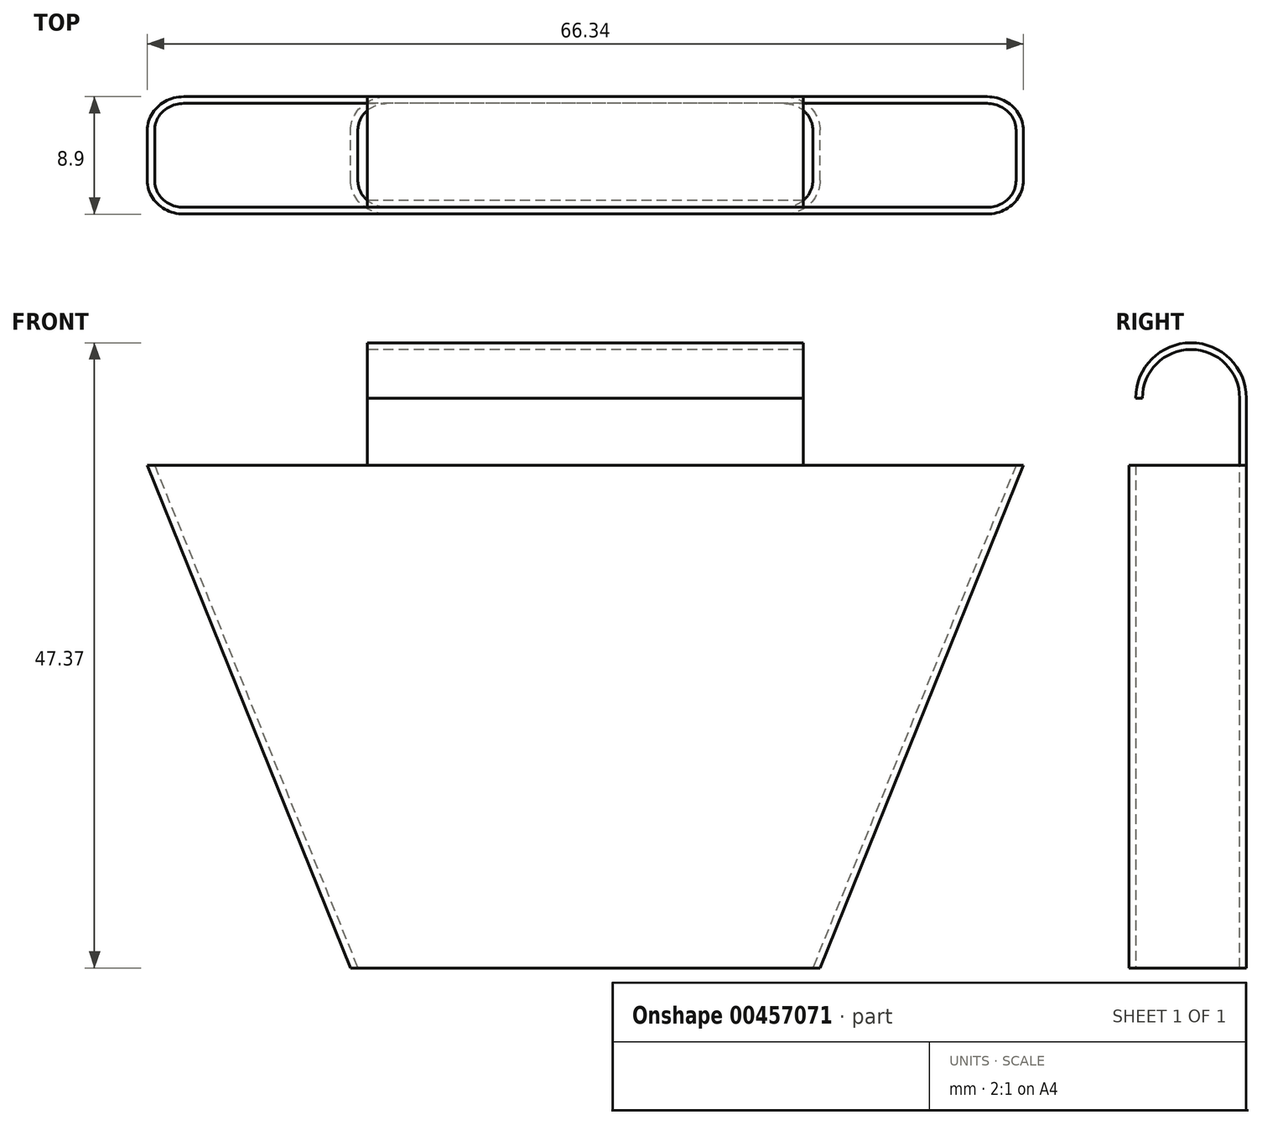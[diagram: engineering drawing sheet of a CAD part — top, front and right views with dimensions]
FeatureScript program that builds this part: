
annotation { "Feature Type Name" : "Feature", "Feature Type Description" : "" }
export const myFeature = defineFeature(function(context is Context, id is Id, definition is map)
    precondition{}
    {
        {
            var Q0;
            Q0=qCreatedBy(makeId("Front.planeOp"),FACE);
            var sketch = newSketch(context, id + "F0", { "sketchPlane" : qUnion([Q0])});
            skLineSegment(sketch, "E0", {"start": v(33.17, 0) * mm, "end": v(17.78, -38.1) * mm});
            skLineSegment(sketch, "E1.MirrorCS", {"start": v(-33.17, 0) * mm, "end": v(-17.78, -38.1) * mm});
            skLineSegment(sketch, "E2", {"start": v(-33.17, 0) * mm, "end": v(33.17, 0) * mm});
            skLineSegment(sketch, "E3", {"start": v(17.78, -38.1) * mm, "end": v(-17.78, -38.1) * mm});
            skLineSegment(sketch, "E4", {"start": v(0, 0) * mm, "end": v(0, -46.38) * mm, "construction": true});
            skSolve(sketch);
        }
        {
            var Q0;
            Q0=qSketchRegion(id+"F0",true);
            extrude(context, id + "F1", {"entities" : qUnion([Q0]), "endBound" : BoundingType.SYMMETRIC, "depth" : 8.9 * mm});
        }
        {
            var Q0;
            Q0=makeQuery(id+"F1.opExtrude","CAP_EDGE",EDGE,{"disambiguationData":[OSD([sQuery(id+"F0.wireOp",EDGE,"E0")])],"isStart":true});
            var Q1;
            Q1=makeQuery(id+"F1.opExtrude","CAP_EDGE",EDGE,{"disambiguationData":[OSD([sQuery(id+"F0.wireOp",EDGE,"E0")])],"isStart":false});
            var Q2;
            Q2=makeQuery(id+"F1.opExtrude","CAP_EDGE",EDGE,{"disambiguationData":[OSD([sQuery(id+"F0.wireOp",EDGE,"E1.MirrorCS")])],"isStart":true});
            var Q3;
            Q3=makeQuery(id+"F1.opExtrude","CAP_EDGE",EDGE,{"disambiguationData":[OSD([sQuery(id+"F0.wireOp",EDGE,"E1.MirrorCS")])],"isStart":false});
            fillet(context, id + "F2", {"entities" : qUnion([Q0, Q1, Q2, Q3]), "radius" : 2.54 * mm, "tangentPropagation" : true, "allowEdgeOverflow" : false});
        }
        {
            var Q0;
            Q0=makeQuery(id+"F1.opExtrude","SWEPT_FACE",FACE,{"disambiguationData":[OSD([sQuery(id+"F0.wireOp",EDGE,"E2")])]});
            var Q1;
            Q1=makeQuery(id+"F1.opExtrude","SWEPT_FACE",FACE,{"disambiguationData":[OSD([sQuery(id+"F0.wireOp",EDGE,"E3")])]});
            shell(context, id + "F3", {"entities" : qUnion([Q0, Q1]), "thickness" : 0.5 * mm});
        }
        {
            var Q0;
            {var subQ0=sQuery(id+"F0.wireOp",EDGE,"E3");var subQ1=sQuery(id+"F0.wireOp",EDGE,"E2");var subQ2=sQuery(id+"F0.wireOp",EDGE,"E1.MirrorCS");var subQ3=sQuery(id+"F0.wireOp",EDGE,"E0");Q0=makeQuery(id+"F3.opShell","OFFSET_FACE",FACE,{"disambiguationData":[OSD([subQ3,subQ2,subQ1,subQ0]),TDD([makeQuery(id+"F1.opExtrude","CAP_FACE",FACE,{"disambiguationData":[OSD([subQ3,subQ2,subQ1,subQ0])],"isStart":false})])]});}
            var sketch = newSketch(context, id + "F4", { "sketchPlane" : qUnion([Q0])});
            skLineSegment(sketch, "E5", {"start": v(0, 0) * mm, "end": v(0, 33.27) * mm, "construction": true});
            skSolve(sketch);
        }
        {
            var Q0;
            Q0=qCreatedBy(makeId("Right.planeOp"),FACE);
            var sketch = newSketch(context, id + "F5", { "sketchPlane" : qUnion([Q0])});
            skLineSegment(sketch, "E6", {"start": v(4.45, 0) * mm, "end": v(4.45, 5.08) * mm});
            skArc(sketch, "E7", {"start": v(4.45, 5.08) * mm, "mid": v(0.25, 9.27) * mm, "end": v(-3.94, 5.08) * mm});
            skArc(sketch, "E8.0", {"start": v(3.94, 5.08) * mm, "mid": v(0.25, 8.76) * mm, "end": v(-3.43, 5.08) * mm});
            skLineSegment(sketch, "E8.1", {"start": v(3.94, 0) * mm, "end": v(3.94, 5.08) * mm});
            skLineSegment(sketch, "E9", {"start": v(3.94, 0) * mm, "end": v(4.45, 0) * mm});
            skLineSegment(sketch, "E10", {"start": v(-3.94, 5.08) * mm, "end": v(-3.43, 5.08) * mm});
            skSolve(sketch);
        }
        {
            var Q0;
            Q0 = qSketchRegion(id + "F5", true);
            extrude(context, id + "F6", {"entities" : qUnion([Q0]), "operationType" : NewBodyOperationType.ADD, "endBound" : BoundingType.SYMMETRIC, "depth" : 33.02 * mm});
        }
    });
